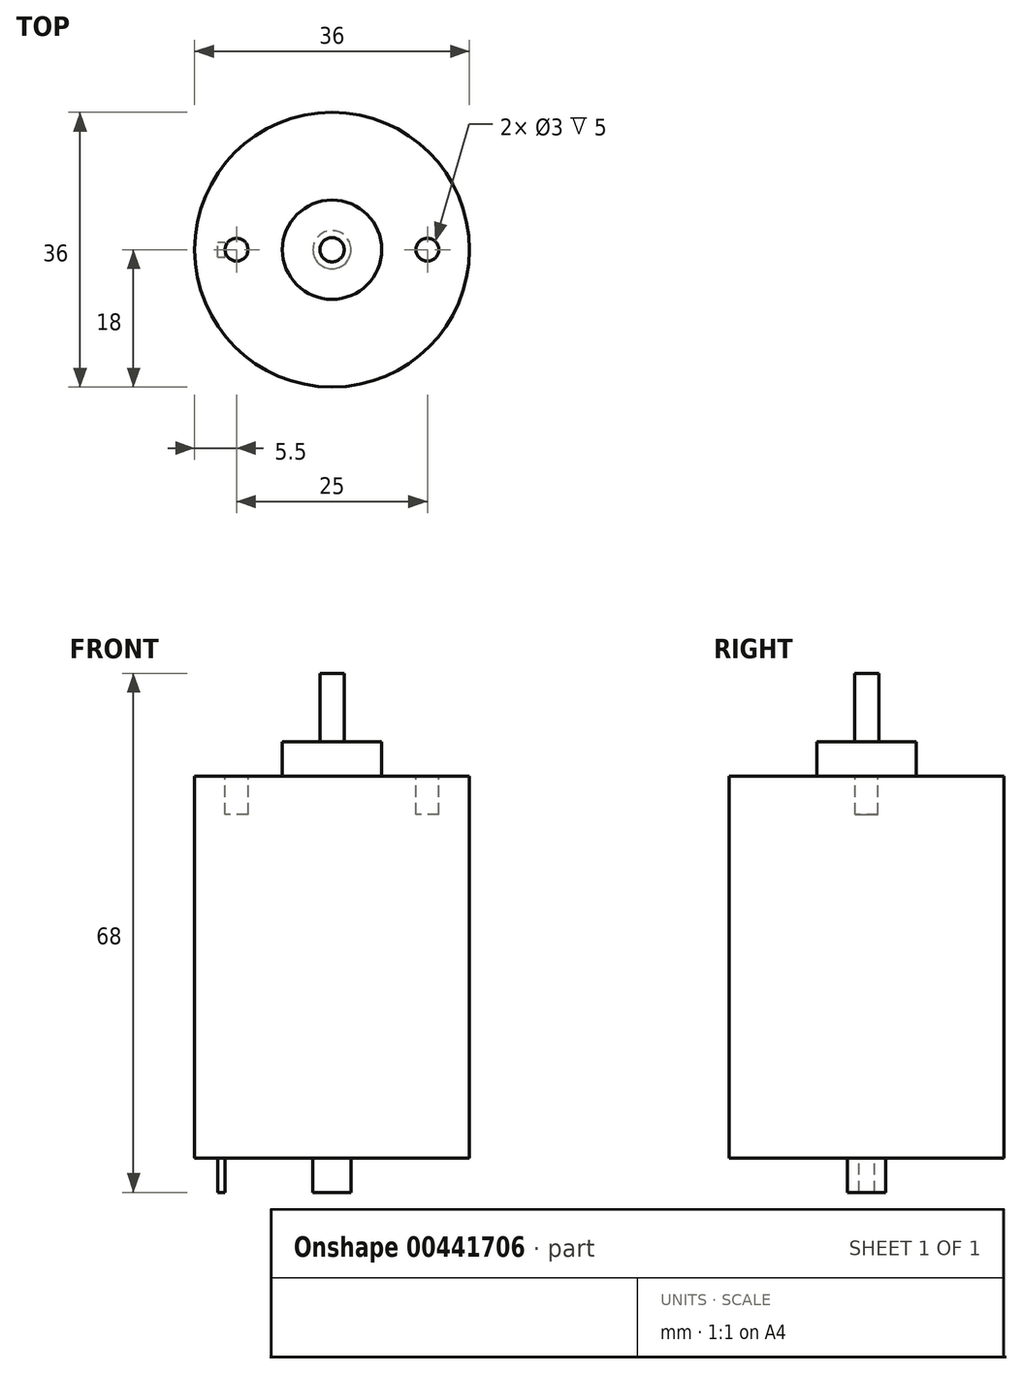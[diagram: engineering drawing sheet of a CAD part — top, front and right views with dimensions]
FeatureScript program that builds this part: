
annotation { "Feature Type Name" : "Feature", "Feature Type Description" : "" }
export const myFeature = defineFeature(function(context is Context, id is Id, definition is map)
    precondition{}
    {
        {
            var Q0;
            Q0=qCreatedBy(makeId("Top.planeOp"),FACE);
            var sketch = newSketch(context, id + "F0", { "sketchPlane" : qUnion([Q0])});
            skCircle(sketch, "E0", {"center": v(0, 0) * mm, "radius": 18 * mm});
            skSolve(sketch);
        }
        {
            var Q0;
            Q0 = qSketchRegion(id + "F0", true);
            extrude(context, id + "F1", {"entities" : qUnion([Q0]), "endBound" : BoundingType.SYMMETRIC, "depth" : 50 * mm});
        }
        {
            var Q0;
            Q0=makeQuery(id+"F1.opExtrude","CAP_FACE",FACE,{"disambiguationData":[OSD([sQuery(id+"F0.wireOp",EDGE,"E0")])],"isStart":false});
            var sketch = newSketch(context, id + "F2", { "sketchPlane" : qUnion([Q0])});
            skCircle(sketch, "E1", {"center": v(0, 0) * mm, "radius": 6.5 * mm});
            skSolve(sketch);
        }
        {
            var Q0;
            Q0 = qSketchRegion(id + "F2", true);
            extrude(context, id + "F3", {"entities" : qUnion([Q0]), "operationType" : NewBodyOperationType.ADD, "depth" : 4.5 * mm});
        }
        {
            var Q0;
            Q0=makeQuery(id+"F3.opExtrude","CAP_FACE",FACE,{"disambiguationData":[OSD([sQuery(id+"F2.wireOp",EDGE,"E1")])],"isStart":false});
            var sketch = newSketch(context, id + "F4", { "sketchPlane" : qUnion([Q0])});
            skCircle(sketch, "E2", {"center": v(0, 0) * mm, "radius": 1.59 * mm});
            skSolve(sketch);
        }
        {
            var Q0;
            Q0 = qSketchRegion(id + "F4", true);
            extrude(context, id + "F5", {"entities" : qUnion([Q0]), "operationType" : NewBodyOperationType.ADD, "depth" : 9 * mm});
        }
        {
            var Q0;
            Q0=makeQuery(id+"F1.opExtrude","CAP_FACE",FACE,{"disambiguationData":[OSD([sQuery(id+"F0.wireOp",EDGE,"E0")])],"isStart":true});
            var sketch = newSketch(context, id + "F6", { "sketchPlane" : qUnion([Q0])});
            skLineSegment(sketch, "E3", {"start": v(-21.52, 0) * mm, "end": v(9.21, 0) * mm, "construction": true});
            skLineSegment(sketch, "E4", {"start": v(0, 7.35) * mm, "end": v(0, -7.2) * mm, "construction": true});
            skLineSegment(sketch, "E5.bottom", {"start": v(-15, 1) * mm, "end": v(-14, 1) * mm});
            skLineSegment(sketch, "E5.top", {"start": v(-15, -1) * mm, "end": v(-14, -1) * mm});
            skLineSegment(sketch, "E5.left", {"start": v(-15, 1) * mm, "end": v(-15, -1) * mm});
            skLineSegment(sketch, "E5.right", {"start": v(-14, 1) * mm, "end": v(-14, -1) * mm});
            skSolve(sketch);
        }
        {
            var Q0;
            Q0 = qSketchRegion(id + "F6", true);
            extrude(context, id + "F7", {"entities" : qUnion([Q0]), "operationType" : NewBodyOperationType.ADD, "depth" : 4.5 * mm});
        }
        {
            var Q0;
            Q0=makeQuery(id+"F1.opExtrude","CAP_FACE",FACE,{"disambiguationData":[OSD([sQuery(id+"F0.wireOp",EDGE,"E0")])],"isStart":false});
            var sketch = newSketch(context, id + "F8", { "sketchPlane" : qUnion([Q0])});
            skLineSegment(sketch, "E6", {"start": v(0, 16.76) * mm, "end": v(0, -14.96) * mm, "construction": true});
            skLineSegment(sketch, "E7", {"start": v(-16.7, 0) * mm, "end": v(17.6, 0) * mm, "construction": true});
            skCircle(sketch, "E8", {"center": v(12.5, 0) * mm, "radius": 1.5 * mm});
            skCircle(sketch, "E9.MirrorC", {"center": v(-12.5, 0) * mm, "radius": 1.5 * mm});
            skSolve(sketch);
        }
        {
            var Q0;
            Q0 = qSketchRegion(id + "F8", true);
            extrude(context, id + "F9", {"entities" : qUnion([Q0]), "operationType" : NewBodyOperationType.REMOVE, "oppositeDirection" : true, "depth" : 5 * mm});
        }
        {
            var Q0;
            Q0=makeQuery(id+"F7.boolean.opBoolean","SPLIT",FACE,{"disambiguationData":[TD([makeQuery(id+"F7.opExtrude","SWEPT_FACE",FACE,{"disambiguationData":[OSD([sQuery(id+"F6.wireOp",EDGE,"JWLlBIxH-fwQi-mrwQ-9IZL-WmM0RiaAhNcl")])]})])],"derivedFrom":makeQuery(id+"F1.opExtrude","CAP_FACE",FACE,{"disambiguationData":[OSD([sQuery(id+"F0.wireOp",EDGE,"E0")])],"isStart":true})});
            var sketch = newSketch(context, id + "F10", { "sketchPlane" : qUnion([Q0])});
            skCircle(sketch, "E10", {"center": v(0, 0) * mm, "radius": 2.5 * mm});
            skSolve(sketch);
        }
        {
            var Q0;
            Q0 = qSketchRegion(id + "F10", true);
            extrude(context, id + "F11", {"entities" : qUnion([Q0]), "operationType" : NewBodyOperationType.ADD, "depth" : 4.5 * mm});
        }
    });
